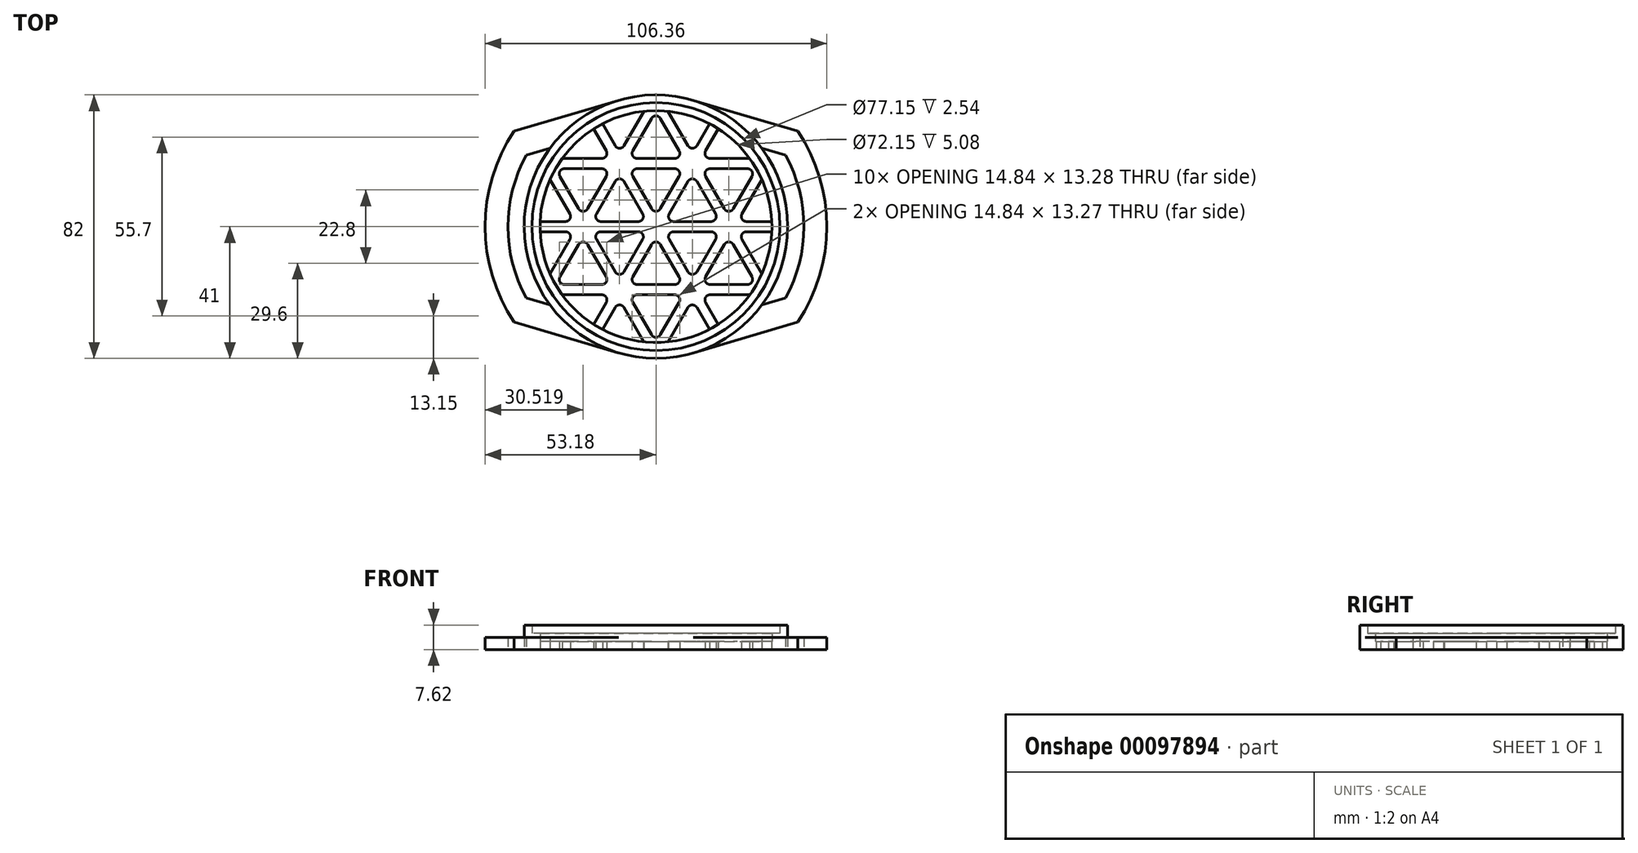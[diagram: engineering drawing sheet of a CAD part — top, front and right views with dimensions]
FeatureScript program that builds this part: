
annotation { "Feature Type Name" : "Feature", "Feature Type Description" : "" }
export const myFeature = defineFeature(function(context is Context, id is Id, definition is map)
    precondition{}
    {
        {
            var Q0;
            Q0=qCreatedBy(makeId("Top.planeOp"),FACE);
            var sketch = newSketch(context, id + "F0", { "sketchPlane" : qUnion([Q0])});
            skCircle(sketch, "E0", {"center": v(0, 0) * mm, "radius": 38.58 * mm});
            skCircle(sketch, "E1", {"center": v(0, 0) * mm, "radius": 41 * mm});
            skCircle(sketch, "E2", {"center": v(0, 0) * mm, "radius": 36.08 * mm});
            skArc(sketch, "E3.cCircle", {"start": v(-7.42, -16.44) * mm, "mid": v(12.1, 13.37) * mm, "end": v(-15.62, -9.02) * mm, "construction": true});
            skLineSegment(sketch, "E3.0", {"start": v(-28.5, 18.04) * mm, "end": v(-16.83, 18.04) * mm});
            skLineSegment(sketch, "E3.1", {"start": v(29.87, 15.66) * mm, "end": v(24.04, 5.56) * mm});
            skLineSegment(sketch, "E3.2", {"start": v(-1.37, -33.7) * mm, "end": v(-7.2, -23.6) * mm});
            skPoint(sketch, "E3.0.midPoint", {"position": v(0, 18.04) * mm});
            skLineSegment(sketch, "E4.0", {"start": v(-36.74, 21.21) * mm, "end": v(-32.22, 21.21) * mm, "construction": true});
            skLineSegment(sketch, "E4.1", {"start": v(0, -42.43) * mm, "end": v(-2.26, -38.5) * mm, "construction": true});
            skLineSegment(sketch, "E4.2", {"start": v(36.74, 21.21) * mm, "end": v(34.48, 17.3) * mm, "construction": true});
            skLineSegment(sketch, "E5", {"start": v(-36.08, 0) * mm, "end": v(36.08, 0) * mm, "construction": true});
            skLineSegment(sketch, "E6.MirrorCS", {"start": v(-36.74, -21.21) * mm, "end": v(-32.22, -21.21) * mm, "construction": true});
            skLineSegment(sketch, "E7.MirrorCS", {"start": v(-28.5, -18.04) * mm, "end": v(-16.83, -18.04) * mm});
            skLineSegment(sketch, "E8.MirrorCS", {"start": v(-1.37, 33.7) * mm, "end": v(-7.2, 23.6) * mm});
            skLineSegment(sketch, "E9.MirrorCS", {"start": v(0, 42.43) * mm, "end": v(-2.26, 38.5) * mm, "construction": true});
            skLineSegment(sketch, "E10.MirrorCS", {"start": v(29.87, -15.66) * mm, "end": v(24.04, -5.56) * mm});
            skLineSegment(sketch, "E11.MirrorCS", {"start": v(36.74, -21.21) * mm, "end": v(34.48, -17.3) * mm, "construction": true});
            skLineSegment(sketch, "E12.trimOffspring", {"start": v(-3.78, 35.88) * mm, "end": v(-9.96, 25.18) * mm});
            skLineSegment(sketch, "E13.trimOffspring", {"start": v(2.26, 38.5) * mm, "end": v(0, 42.43) * mm, "construction": true});
            skLineSegment(sketch, "E14.trimOffspring", {"start": v(-29.18, 21.21) * mm, "end": v(-16.83, 21.21) * mm});
            skLineSegment(sketch, "E15.trimOffspring", {"start": v(-34.48, 17.3) * mm, "end": v(-36.74, 21.21) * mm, "construction": true});
            skLineSegment(sketch, "E16.trimOffspring", {"start": v(-34.48, -17.3) * mm, "end": v(-36.74, -21.21) * mm, "construction": true});
            skLineSegment(sketch, "E17.trimOffspring", {"start": v(-29.18, -21.21) * mm, "end": v(-16.83, -21.21) * mm});
            skLineSegment(sketch, "E18.trimOffspring", {"start": v(32.22, 21.21) * mm, "end": v(36.74, 21.21) * mm, "construction": true});
            skLineSegment(sketch, "E19.trimOffspring", {"start": v(32.96, 14.66) * mm, "end": v(26.79, 3.97) * mm});
            skLineSegment(sketch, "E20.trimOffspring", {"start": v(32.22, -21.21) * mm, "end": v(36.74, -21.21) * mm, "construction": true});
            skLineSegment(sketch, "E21.trimOffspring", {"start": v(32.96, -14.66) * mm, "end": v(26.79, -3.97) * mm});
            skLineSegment(sketch, "E22.trimOffspring", {"start": v(-3.78, -35.88) * mm, "end": v(-9.96, -25.18) * mm});
            skLineSegment(sketch, "E23.trimOffspring", {"start": v(2.26, -38.5) * mm, "end": v(0, -42.43) * mm, "construction": true});
            skLineSegment(sketch, "E24.rect.bottom", {"start": v(-40.32, 22.22) * mm, "end": v(40.32, 22.22) * mm, "construction": true});
            skLineSegment(sketch, "E24.rect.top", {"start": v(-40.32, -22.22) * mm, "end": v(40.32, -22.22) * mm, "construction": true});
            skLineSegment(sketch, "E24.rect.left", {"start": v(-40.32, 22.23) * mm, "end": v(-40.32, -22.23) * mm, "construction": true});
            skLineSegment(sketch, "E24.rect.right", {"start": v(40.32, 22.23) * mm, "end": v(40.32, -22.23) * mm, "construction": true});
            skArc(sketch, "E25", {"start": v(-44.13, 29.68) * mm, "mid": v(-53.18, 0) * mm, "end": v(-44.13, -29.68) * mm});
            skLineSegment(sketch, "E26", {"start": v(-44.13, 29.68) * mm, "end": v(-44.13, -29.68) * mm, "construction": true});
            skLineSegment(sketch, "E27", {"start": v(-44.13, -29.68) * mm, "end": v(-31.73, -33.36) * mm});
            skLineSegment(sketch, "E28", {"start": v(-11.65, 39.3) * mm, "end": v(-31.73, 33.36) * mm});
            skPoint(sketch, "E29.orphan", {"position": v(0, -42.76) * mm});
            skPoint(sketch, "E30.orphan", {"position": v(0, 42.76) * mm});
            skLineSegment(sketch, "E31", {"start": v(-31.73, -33.36) * mm, "end": v(-11.65, -39.3) * mm});
            skLineSegment(sketch, "E32", {"start": v(-31.73, 33.36) * mm, "end": v(-44.13, 29.68) * mm});
            skArc(sketch, "E33", {"start": v(-44.13, -13.12) * mm, "mid": v(-39.25, -24.05) * mm, "end": v(-31.73, -33.36) * mm});
            skArc(sketch, "E34", {"start": v(-44.13, 13.12) * mm, "mid": v(-46.04, 0) * mm, "end": v(-44.13, -13.12) * mm});
            skLineSegment(sketch, "E35", {"start": v(0, 36.07) * mm, "end": v(0, -36.07) * mm, "construction": true});
            skLineSegment(sketch, "E36.MirrorCS", {"start": v(44.13, 29.68) * mm, "end": v(44.13, -29.68) * mm, "construction": true});
            skLineSegment(sketch, "E37.MirrorCS", {"start": v(11.65, 39.3) * mm, "end": v(31.73, 33.36) * mm});
            skLineSegment(sketch, "E38.MirrorCS", {"start": v(31.73, -33.36) * mm, "end": v(11.65, -39.3) * mm});
            skLineSegment(sketch, "E39.MirrorCS", {"start": v(44.13, -29.68) * mm, "end": v(31.73, -33.36) * mm});
            skLineSegment(sketch, "E40.MirrorCS", {"start": v(31.73, 33.36) * mm, "end": v(44.13, 29.68) * mm});
            skArc(sketch, "E41.trimOffspring", {"start": v(-31.73, 33.36) * mm, "mid": v(-39.25, 24.05) * mm, "end": v(-44.13, 13.12) * mm});
            skArc(sketch, "E42.trimOffspring", {"start": v(31.73, -33.36) * mm, "mid": v(46.04, 0) * mm, "end": v(31.73, 33.36) * mm});
            skArc(sketch, "E43.trimOffspring", {"start": v(44.13, -29.68) * mm, "mid": v(53.18, 0) * mm, "end": v(44.13, 29.68) * mm});
            skLineSegment(sketch, "E44", {"start": v(-40.32, 22.22) * mm, "end": v(-32.94, 24.41) * mm});
            skLineSegment(sketch, "E45.MirrorCS", {"start": v(40.32, 22.22) * mm, "end": v(32.94, 24.41) * mm});
            skLineSegment(sketch, "E46.MirrorCS", {"start": v(-40.32, -22.22) * mm, "end": v(-32.94, -24.41) * mm});
            skLineSegment(sketch, "E47.MirrorCS", {"start": v(40.32, -22.22) * mm, "end": v(32.94, -24.41) * mm});
            skLineSegment(sketch, "E48.trimOffspring", {"start": v(-26.79, -3.97) * mm, "end": v(-32.96, -14.66) * mm});
            skLineSegment(sketch, "E49.trimOffspring", {"start": v(-24.04, -5.56) * mm, "end": v(-29.87, -15.66) * mm});
            skLineSegment(sketch, "E50.trimOffspring", {"start": v(-24.04, 5.56) * mm, "end": v(-29.87, 15.66) * mm});
            skLineSegment(sketch, "E51.trimOffspring", {"start": v(-26.79, 3.97) * mm, "end": v(-32.96, 14.66) * mm});
            skLineSegment(sketch, "E52.trimOffspring", {"start": v(-5.83, 18.04) * mm, "end": v(5.83, 18.04) * mm});
            skLineSegment(sketch, "E53.trimOffspring", {"start": v(-5.83, 21.21) * mm, "end": v(5.83, 21.21) * mm});
            skLineSegment(sketch, "E54.trimOffspring", {"start": v(-15.45, 15.66) * mm, "end": v(-21.29, 5.56) * mm});
            skLineSegment(sketch, "E55.trimOffspring", {"start": v(-12.7, 14.07) * mm, "end": v(-18.54, 3.97) * mm});
            skLineSegment(sketch, "E56.trimOffspring", {"start": v(7.2, 23.6) * mm, "end": v(1.37, 33.7) * mm});
            skLineSegment(sketch, "E57.trimOffspring", {"start": v(9.96, 25.18) * mm, "end": v(3.78, 35.88) * mm});
            skLineSegment(sketch, "E58.trimOffspring", {"start": v(16.83, 18.04) * mm, "end": v(28.5, 18.04) * mm});
            skLineSegment(sketch, "E59.trimOffspring", {"start": v(16.83, 21.21) * mm, "end": v(29.18, 21.21) * mm});
            skLineSegment(sketch, "E60.trimOffspring", {"start": v(21.29, -5.56) * mm, "end": v(15.45, -15.66) * mm});
            skLineSegment(sketch, "E61.trimOffspring", {"start": v(18.54, -3.97) * mm, "end": v(12.7, -14.07) * mm});
            skLineSegment(sketch, "E62.trimOffspring", {"start": v(16.83, -21.21) * mm, "end": v(29.18, -21.21) * mm});
            skLineSegment(sketch, "E63.trimOffspring", {"start": v(16.83, -18.04) * mm, "end": v(28.5, -18.04) * mm});
            skLineSegment(sketch, "E64.trimOffspring", {"start": v(-12.7, -14.07) * mm, "end": v(-18.54, -3.97) * mm});
            skLineSegment(sketch, "E65.trimOffspring", {"start": v(-15.45, -15.66) * mm, "end": v(-21.29, -5.56) * mm});
            skLineSegment(sketch, "E66.trimOffspring", {"start": v(-5.83, -18.04) * mm, "end": v(5.83, -18.04) * mm});
            skLineSegment(sketch, "E67.trimOffspring", {"start": v(-5.83, -21.21) * mm, "end": v(5.83, -21.21) * mm});
            skLineSegment(sketch, "E68.trimOffspring", {"start": v(7.2, -23.6) * mm, "end": v(1.37, -33.7) * mm});
            skLineSegment(sketch, "E69.trimOffspring", {"start": v(9.96, -25.18) * mm, "end": v(3.78, -35.88) * mm});
            skLineSegment(sketch, "E70.trimOffspring", {"start": v(18.54, 3.97) * mm, "end": v(12.7, 14.07) * mm});
            skLineSegment(sketch, "E71.trimOffspring", {"start": v(21.29, 5.56) * mm, "end": v(15.45, 15.66) * mm});
            skPoint(sketch, "E72.visualSharp", {"position": v(-31.24, 18.04) * mm});
            skArc(sketch, "E72.filletArc", {"start": v(-28.5, 18.04) * mm, "mid": v(-29.87, 17.24) * mm, "end": v(-29.87, 15.66) * mm});
            skPoint(sketch, "E73.visualSharp", {"position": v(0, 36.07) * mm});
            skArc(sketch, "E73.filletArc", {"start": v(1.37, 33.7) * mm, "mid": v(0, 34.49) * mm, "end": v(-1.37, 33.7) * mm});
            skPoint(sketch, "E74.visualSharp", {"position": v(31.24, 18.04) * mm});
            skArc(sketch, "E74.filletArc", {"start": v(29.87, 15.66) * mm, "mid": v(29.87, 17.24) * mm, "end": v(28.5, 18.04) * mm});
            skPoint(sketch, "E75.visualSharp", {"position": v(31.24, -18.04) * mm});
            skArc(sketch, "E75.filletArc", {"start": v(28.5, -18.04) * mm, "mid": v(29.87, -17.24) * mm, "end": v(29.87, -15.66) * mm});
            skPoint(sketch, "E76.visualSharp", {"position": v(0, -36.07) * mm});
            skArc(sketch, "E76.filletArc", {"start": v(-1.37, -33.7) * mm, "mid": v(0, -34.49) * mm, "end": v(1.37, -33.7) * mm});
            skPoint(sketch, "E77.visualSharp", {"position": v(-31.24, -18.04) * mm});
            skArc(sketch, "E77.filletArc", {"start": v(-29.87, -15.66) * mm, "mid": v(-29.87, -17.24) * mm, "end": v(-28.5, -18.04) * mm});
            skPoint(sketch, "E78.visualSharp", {"position": v(-22.66, -3.18) * mm});
            skArc(sketch, "E78.filletArc", {"start": v(-21.29, -5.56) * mm, "mid": v(-22.66, -4.76) * mm, "end": v(-24.04, -5.56) * mm});
            skPoint(sketch, "E79.visualSharp", {"position": v(-14.08, -18.04) * mm});
            skArc(sketch, "E79.filletArc", {"start": v(-16.83, -18.04) * mm, "mid": v(-15.45, -17.24) * mm, "end": v(-15.45, -15.66) * mm});
            skPoint(sketch, "E80.visualSharp", {"position": v(-12.25, -21.21) * mm});
            skPoint(sketch, "E81.visualSharp", {"position": v(-8.58, -21.21) * mm});
            skArc(sketch, "E81.filletArc", {"start": v(-5.83, -21.21) * mm, "mid": v(-7.2, -22) * mm, "end": v(-7.2, -23.6) * mm});
            skPoint(sketch, "E82.visualSharp", {"position": v(8.58, -21.21) * mm});
            skArc(sketch, "E82.filletArc", {"start": v(7.2, -23.6) * mm, "mid": v(7.2, -22) * mm, "end": v(5.83, -21.21) * mm});
            skPoint(sketch, "E83.visualSharp", {"position": v(14.08, -18.04) * mm});
            skArc(sketch, "E83.filletArc", {"start": v(15.45, -15.66) * mm, "mid": v(15.45, -17.24) * mm, "end": v(16.83, -18.04) * mm});
            skPoint(sketch, "E84.visualSharp", {"position": v(22.66, -3.18) * mm});
            skArc(sketch, "E84.filletArc", {"start": v(24.04, -5.56) * mm, "mid": v(22.66, -4.76) * mm, "end": v(21.29, -5.56) * mm});
            skPoint(sketch, "E85.visualSharp", {"position": v(22.66, 3.18) * mm});
            skArc(sketch, "E85.filletArc", {"start": v(21.29, 5.56) * mm, "mid": v(22.66, 4.76) * mm, "end": v(24.04, 5.56) * mm});
            skPoint(sketch, "E86.visualSharp", {"position": v(8.58, 21.21) * mm});
            skArc(sketch, "E86.filletArc", {"start": v(5.83, 21.21) * mm, "mid": v(7.2, 22) * mm, "end": v(7.2, 23.6) * mm});
            skPoint(sketch, "E87.visualSharp", {"position": v(14.08, 18.04) * mm});
            skArc(sketch, "E87.filletArc", {"start": v(16.83, 18.04) * mm, "mid": v(15.45, 17.24) * mm, "end": v(15.45, 15.66) * mm});
            skPoint(sketch, "E88.visualSharp", {"position": v(-8.58, 21.21) * mm});
            skArc(sketch, "E88.filletArc", {"start": v(-7.2, 23.6) * mm, "mid": v(-7.2, 22) * mm, "end": v(-5.83, 21.21) * mm});
            skPoint(sketch, "E89.visualSharp", {"position": v(-14.08, 18.04) * mm});
            skArc(sketch, "E89.filletArc", {"start": v(-15.45, 15.66) * mm, "mid": v(-15.45, 17.24) * mm, "end": v(-16.83, 18.04) * mm});
            skPoint(sketch, "E90.visualSharp", {"position": v(-22.66, 3.18) * mm});
            skArc(sketch, "E90.filletArc", {"start": v(-24.04, 5.56) * mm, "mid": v(-22.66, 4.76) * mm, "end": v(-21.29, 5.56) * mm});
            skPoint(sketch, "E91.visualSharp", {"position": v(-24.5, 0) * mm});
            skPoint(sketch, "E92.visualSharp", {"position": v(12.25, -21.21) * mm});
            skPoint(sketch, "E93.visualSharp", {"position": v(24.5, 0) * mm});
            skPoint(sketch, "E94.visualSharp", {"position": v(12.25, 21.21) * mm});
            skPoint(sketch, "E95.visualSharp", {"position": v(-12.25, 21.21) * mm});
            skPoint(sketch, "E96.visualSharp", {"position": v(-20.83, 0) * mm});
            skPoint(sketch, "E97.visualSharp", {"position": v(-10.41, 18.04) * mm});
            skPoint(sketch, "E98.visualSharp", {"position": v(10.41, 18.04) * mm});
            skPoint(sketch, "E99.visualSharp", {"position": v(20.83, 0) * mm});
            skPoint(sketch, "E100.visualSharp", {"position": v(10.41, -18.04) * mm});
            skPoint(sketch, "E101.visualSharp", {"position": v(-10.41, -18.04) * mm});
            skLineSegment(sketch, "E102", {"start": v(36.04, 1.59) * mm, "end": v(28.16, 1.59) * mm});
            skLineSegment(sketch, "E103.MirrorCS", {"start": v(36.04, -1.59) * mm, "end": v(28.16, -1.59) * mm});
            skPoint(sketch, "E104.orphan", {"position": v(-38.54, 1.59) * mm});
            skPoint(sketch, "E105.orphan", {"position": v(-38.54, -1.59) * mm});
            skLineSegment(sketch, "E106.1.0", {"start": v(-19.4, 30.42) * mm, "end": v(-15.45, 23.6) * mm});
            skLineSegment(sketch, "E106.1.1", {"start": v(-16.65, 32) * mm, "end": v(-12.7, 25.18) * mm});
            skLineSegment(sketch, "E106.2.0", {"start": v(-16.65, -32) * mm, "end": v(-12.7, -25.18) * mm});
            skLineSegment(sketch, "E106.2.1", {"start": v(-19.4, -30.42) * mm, "end": v(-15.45, -23.6) * mm});
            skLineSegment(sketch, "E107.trimOffspring", {"start": v(1.37, 5.56) * mm, "end": v(7.2, 15.66) * mm});
            skLineSegment(sketch, "E108.trimOffspring", {"start": v(-5.5, 1.59) * mm, "end": v(-17.16, 1.59) * mm});
            skLineSegment(sketch, "E109.trimOffspring", {"start": v(4.12, 3.97) * mm, "end": v(9.96, 14.07) * mm});
            skLineSegment(sketch, "E110.trimOffspring", {"start": v(1.37, -5.56) * mm, "end": v(7.2, -15.66) * mm});
            skLineSegment(sketch, "E111.trimOffspring", {"start": v(-5.5, -1.59) * mm, "end": v(-17.16, -1.59) * mm});
            skLineSegment(sketch, "E112.trimOffspring", {"start": v(4.12, -3.97) * mm, "end": v(9.96, -14.07) * mm});
            skLineSegment(sketch, "E113", {"start": v(-9.96, -14.07) * mm, "end": v(-4.12, -3.97) * mm});
            skLineSegment(sketch, "E114.trimOffspring", {"start": v(-9.96, 14.07) * mm, "end": v(-4.12, 3.97) * mm});
            skLineSegment(sketch, "E115.trimOffspring", {"start": v(-7.2, 15.66) * mm, "end": v(-1.37, 5.56) * mm});
            skLineSegment(sketch, "E116.trimOffspring", {"start": v(12.7, 25.18) * mm, "end": v(16.65, 32) * mm});
            skLineSegment(sketch, "E117.trimOffspring", {"start": v(15.45, 23.6) * mm, "end": v(19.4, 30.42) * mm});
            skLineSegment(sketch, "E118.trimOffspring", {"start": v(17.16, 1.59) * mm, "end": v(5.5, 1.59) * mm});
            skLineSegment(sketch, "E119.trimOffspring", {"start": v(17.16, -1.59) * mm, "end": v(5.5, -1.59) * mm});
            skLineSegment(sketch, "E120.trimOffspring", {"start": v(12.7, -25.18) * mm, "end": v(16.65, -32) * mm});
            skLineSegment(sketch, "E121.trimOffspring", {"start": v(15.45, -23.6) * mm, "end": v(19.4, -30.42) * mm});
            skLineSegment(sketch, "E122.trimOffspring", {"start": v(-7.2, -15.66) * mm, "end": v(-1.37, -5.56) * mm});
            skLineSegment(sketch, "E123.trimOffspring", {"start": v(-28.16, -1.59) * mm, "end": v(-36.04, -1.59) * mm});
            skLineSegment(sketch, "E124.trimOffspring", {"start": v(-28.16, 1.59) * mm, "end": v(-36.04, 1.59) * mm});
            skPoint(sketch, "E125.visualSharp", {"position": v(11.33, 22.8) * mm});
            skArc(sketch, "E125.filletArc", {"start": v(9.96, 25.18) * mm, "mid": v(11.33, 24.39) * mm, "end": v(12.7, 25.18) * mm});
            skPoint(sketch, "E126.visualSharp", {"position": v(25.41, -1.59) * mm});
            skArc(sketch, "E126.filletArc", {"start": v(28.16, -1.59) * mm, "mid": v(26.79, -2.38) * mm, "end": v(26.79, -3.97) * mm});
            skPoint(sketch, "E127.visualSharp", {"position": v(14.08, -21.21) * mm});
            skArc(sketch, "E127.filletArc", {"start": v(16.83, -21.21) * mm, "mid": v(15.45, -22) * mm, "end": v(15.45, -23.6) * mm});
            skPoint(sketch, "E128.visualSharp", {"position": v(-11.33, -22.8) * mm});
            skArc(sketch, "E128.filletArc", {"start": v(-9.96, -25.18) * mm, "mid": v(-11.33, -24.39) * mm, "end": v(-12.7, -25.18) * mm});
            skPoint(sketch, "E129.visualSharp", {"position": v(11.33, -22.8) * mm});
            skArc(sketch, "E129.filletArc", {"start": v(12.7, -25.18) * mm, "mid": v(11.33, -24.39) * mm, "end": v(9.96, -25.18) * mm});
            skPoint(sketch, "E130.visualSharp", {"position": v(-14.08, -21.21) * mm});
            skArc(sketch, "E130.filletArc", {"start": v(-15.45, -23.6) * mm, "mid": v(-15.45, -22) * mm, "end": v(-16.83, -21.21) * mm});
            skPoint(sketch, "E131.visualSharp", {"position": v(-25.41, 1.59) * mm});
            skArc(sketch, "E131.filletArc", {"start": v(-28.16, 1.59) * mm, "mid": v(-26.79, 2.38) * mm, "end": v(-26.79, 3.97) * mm});
            skPoint(sketch, "E132.visualSharp", {"position": v(-25.41, -1.59) * mm});
            skArc(sketch, "E132.filletArc", {"start": v(-26.79, -3.97) * mm, "mid": v(-26.79, -2.38) * mm, "end": v(-28.16, -1.59) * mm});
            skPoint(sketch, "E133.visualSharp", {"position": v(-11.33, 22.8) * mm});
            skArc(sketch, "E133.filletArc", {"start": v(-12.7, 25.18) * mm, "mid": v(-11.33, 24.39) * mm, "end": v(-9.96, 25.18) * mm});
            skPoint(sketch, "E134.visualSharp", {"position": v(-14.08, 21.21) * mm});
            skArc(sketch, "E134.filletArc", {"start": v(-16.83, 21.21) * mm, "mid": v(-15.45, 22) * mm, "end": v(-15.45, 23.6) * mm});
            skPoint(sketch, "E135.visualSharp", {"position": v(14.08, 21.21) * mm});
            skArc(sketch, "E135.filletArc", {"start": v(15.45, 23.6) * mm, "mid": v(15.45, 22) * mm, "end": v(16.83, 21.21) * mm});
            skPoint(sketch, "E136.visualSharp", {"position": v(25.41, 1.59) * mm});
            skArc(sketch, "E136.filletArc", {"start": v(26.79, 3.97) * mm, "mid": v(26.79, 2.38) * mm, "end": v(28.16, 1.59) * mm});
            skPoint(sketch, "E137.visualSharp", {"position": v(11.33, -16.45) * mm});
            skArc(sketch, "E137.filletArc", {"start": v(9.96, -14.07) * mm, "mid": v(11.33, -14.86) * mm, "end": v(12.7, -14.07) * mm});
            skPoint(sketch, "E138.visualSharp", {"position": v(2.75, -1.59) * mm});
            skArc(sketch, "E138.filletArc", {"start": v(5.5, -1.59) * mm, "mid": v(4.12, -2.38) * mm, "end": v(4.12, -3.97) * mm});
            skPoint(sketch, "E139.visualSharp", {"position": v(19.91, -1.59) * mm});
            skArc(sketch, "E139.filletArc", {"start": v(18.54, -3.97) * mm, "mid": v(18.54, -2.38) * mm, "end": v(17.16, -1.59) * mm});
            skPoint(sketch, "E140.visualSharp", {"position": v(19.91, 1.59) * mm});
            skArc(sketch, "E140.filletArc", {"start": v(17.16, 1.59) * mm, "mid": v(18.54, 2.38) * mm, "end": v(18.54, 3.97) * mm});
            skPoint(sketch, "E141.visualSharp", {"position": v(11.33, 16.45) * mm});
            skArc(sketch, "E141.filletArc", {"start": v(12.7, 14.07) * mm, "mid": v(11.33, 14.86) * mm, "end": v(9.96, 14.07) * mm});
            skPoint(sketch, "E142.visualSharp", {"position": v(2.75, 1.59) * mm});
            skArc(sketch, "E142.filletArc", {"start": v(4.12, 3.97) * mm, "mid": v(4.12, 2.38) * mm, "end": v(5.5, 1.59) * mm});
            skPoint(sketch, "E143.visualSharp", {"position": v(8.58, 18.04) * mm});
            skArc(sketch, "E143.filletArc", {"start": v(7.2, 15.66) * mm, "mid": v(7.2, 17.24) * mm, "end": v(5.83, 18.04) * mm});
            skPoint(sketch, "E144.visualSharp", {"position": v(-8.58, 18.04) * mm});
            skArc(sketch, "E144.filletArc", {"start": v(-5.83, 18.04) * mm, "mid": v(-7.2, 17.24) * mm, "end": v(-7.2, 15.66) * mm});
            skPoint(sketch, "E145.visualSharp", {"position": v(0, 3.17) * mm});
            skArc(sketch, "E145.filletArc", {"start": v(-1.37, 5.56) * mm, "mid": v(0, 4.76) * mm, "end": v(1.37, 5.56) * mm});
            skPoint(sketch, "E146.visualSharp", {"position": v(-2.75, 1.59) * mm});
            skArc(sketch, "E146.filletArc", {"start": v(-5.5, 1.59) * mm, "mid": v(-4.12, 2.38) * mm, "end": v(-4.12, 3.97) * mm});
            skPoint(sketch, "E147.visualSharp", {"position": v(-11.33, 16.45) * mm});
            skArc(sketch, "E147.filletArc", {"start": v(-9.96, 14.07) * mm, "mid": v(-11.33, 14.86) * mm, "end": v(-12.7, 14.07) * mm});
            skPoint(sketch, "E148.visualSharp", {"position": v(-19.91, 1.59) * mm});
            skArc(sketch, "E148.filletArc", {"start": v(-18.54, 3.97) * mm, "mid": v(-18.54, 2.38) * mm, "end": v(-17.16, 1.59) * mm});
            skPoint(sketch, "E149.visualSharp", {"position": v(-2.75, -1.59) * mm});
            skArc(sketch, "E149.filletArc", {"start": v(-4.12, -3.97) * mm, "mid": v(-4.12, -2.38) * mm, "end": v(-5.5, -1.59) * mm});
            skPoint(sketch, "E150.visualSharp", {"position": v(-19.91, -1.59) * mm});
            skArc(sketch, "E150.filletArc", {"start": v(-17.16, -1.59) * mm, "mid": v(-18.54, -2.38) * mm, "end": v(-18.54, -3.97) * mm});
            skPoint(sketch, "E151.visualSharp", {"position": v(-8.58, -18.04) * mm});
            skArc(sketch, "E151.filletArc", {"start": v(-7.2, -15.66) * mm, "mid": v(-7.2, -17.24) * mm, "end": v(-5.83, -18.04) * mm});
            skPoint(sketch, "E152.visualSharp", {"position": v(0, -3.18) * mm});
            skArc(sketch, "E152.filletArc", {"start": v(1.37, -5.56) * mm, "mid": v(0, -4.76) * mm, "end": v(-1.37, -5.56) * mm});
            skPoint(sketch, "E153.visualSharp", {"position": v(8.58, -18.04) * mm});
            skArc(sketch, "E153.filletArc", {"start": v(5.83, -18.04) * mm, "mid": v(7.2, -17.24) * mm, "end": v(7.2, -15.66) * mm});
            skArc(sketch, "E154.filletArc", {"start": v(-12.7, -14.07) * mm, "mid": v(-11.33, -14.86) * mm, "end": v(-9.96, -14.07) * mm});
            skCircle(sketch, "E155", {"center": v(0, 0) * mm, "radius": 6.35 * mm, "construction": true});
            skSolve(sketch);
        }
        {
            var Q0;
            Q0=makeQuery(id+"F0.imprint","IMPRINT",FACE,{"disambiguationData":[TD([[makeQuery(id+"F0.imprint","IMPRINT",EDGE,{"derivedFrom":sQuery(id+"F0.wireOp",EDGE,"E0")}),-1.0]])]});
            extrude(context, id + "F1", {"entities" : qUnion([Q0]), "depth" : 7.62 * mm});
        }
        {
            var Q0;
            Q0=makeQuery(id+"F0.imprint","IMPRINT",FACE,{"disambiguationData":[TD([[makeQuery(id+"F0.imprint","IMPRINT",EDGE,{"derivedFrom":sQuery(id+"F0.wireOp",EDGE,"E0")}),1.0]])]});
            extrude(context, id + "F2", {"entities" : qUnion([Q0]), "operationType" : NewBodyOperationType.ADD, "depth" : 5.08 * mm});
        }
        {
            var Q0;
            {var subQ22=sQuery(id+"F0.wireOp",EDGE,"E3.0");Q0=makeQuery(id+"F0.imprint","IMPRINT",FACE,{"disambiguationData":[TD([[makeQuery(id+"F0.imprint","IMPRINT",EDGE,{"derivedFrom":subQ22}),1.0]])]});}
            var Q1;
            Q1=makeQuery(id+"F0.imprint","IMPRINT",FACE,{"disambiguationData":[TD([[makeQuery(id+"F0.imprint","IMPRINT",EDGE,{"derivedFrom":sQuery(id+"F0.wireOp",EDGE,"E25")}),1.0]])]});
            var Q2;
            {var subQ2=sQuery(id+"F0.wireOp",EDGE,"E31");Q2=makeQuery(id+"F0.imprint","IMPRINT",FACE,{"disambiguationData":[TD([[makeQuery(id+"F0.imprint","IMPRINT",EDGE,{"derivedFrom":subQ2}),1.0]])]});}
            var Q3;
            {var subQ2=sQuery(id+"F0.wireOp",EDGE,"E28");Q3=makeQuery(id+"F0.imprint","IMPRINT",FACE,{"disambiguationData":[TD([[makeQuery(id+"F0.imprint","IMPRINT",EDGE,{"derivedFrom":subQ2}),1.0]])]});}
            var Q4;
            {var subQ2=sQuery(id+"F0.wireOp",EDGE,"E37.MirrorCS");Q4=makeQuery(id+"F0.imprint","IMPRINT",FACE,{"disambiguationData":[TD([[makeQuery(id+"F0.imprint","IMPRINT",EDGE,{"derivedFrom":subQ2}),-1.0]])]});}
            var Q5;
            {var subQ4=sQuery(id+"F0.wireOp",EDGE,"E39.MirrorCS");Q5=makeQuery(id+"F0.imprint","IMPRINT",FACE,{"disambiguationData":[TD([[makeQuery(id+"F0.imprint","IMPRINT",EDGE,{"derivedFrom":subQ4}),-1.0]])]});}
            var Q6;
            {var subQ2=sQuery(id+"F0.wireOp",EDGE,"E38.MirrorCS");Q6=makeQuery(id+"F0.imprint","IMPRINT",FACE,{"disambiguationData":[TD([[makeQuery(id+"F0.imprint","IMPRINT",EDGE,{"derivedFrom":subQ2}),-1.0]])]});}
            extrude(context, id + "F3", {"entities" : qUnion([Q0, Q1, Q2, Q3, Q4, Q5, Q6]), "operationType" : NewBodyOperationType.ADD, "depth" : 3.8 * mm});
        }
        {
            var Q0;
            Q0=makeQuery(id+"F3.opExtrude","CAP_FACE",FACE,{"disambiguationData":[OSD([sQuery(id+"F0.wireOp",EDGE,"E2"),sQuery(id+"F0.wireOp",EDGE,"E3.0"),sQuery(id+"F0.wireOp",EDGE,"E3.1"),sQuery(id+"F0.wireOp",EDGE,"E3.2"),sQuery(id+"F0.wireOp",EDGE,"E7.MirrorCS"),sQuery(id+"F0.wireOp",EDGE,"E8.MirrorCS"),sQuery(id+"F0.wireOp",EDGE,"E10.MirrorCS"),sQuery(id+"F0.wireOp",EDGE,"E12.trimOffspring"),sQuery(id+"F0.wireOp",EDGE,"E14.trimOffspring"),sQuery(id+"F0.wireOp",EDGE,"E17.trimOffspring"),sQuery(id+"F0.wireOp",EDGE,"E19.trimOffspring"),sQuery(id+"F0.wireOp",EDGE,"E21.trimOffspring"),sQuery(id+"F0.wireOp",EDGE,"E22.trimOffspring"),sQuery(id+"F0.wireOp",EDGE,"E48.trimOffspring"),sQuery(id+"F0.wireOp",EDGE,"E49.trimOffspring"),sQuery(id+"F0.wireOp",EDGE,"E50.trimOffspring"),sQuery(id+"F0.wireOp",EDGE,"E51.trimOffspring"),sQuery(id+"F0.wireOp",EDGE,"E52.trimOffspring"),sQuery(id+"F0.wireOp",EDGE,"E53.trimOffspring"),sQuery(id+"F0.wireOp",EDGE,"E54.trimOffspring"),sQuery(id+"F0.wireOp",EDGE,"E55.trimOffspring"),sQuery(id+"F0.wireOp",EDGE,"E56.trimOffspring"),sQuery(id+"F0.wireOp",EDGE,"E57.trimOffspring"),sQuery(id+"F0.wireOp",EDGE,"E58.trimOffspring"),sQuery(id+"F0.wireOp",EDGE,"E59.trimOffspring"),sQuery(id+"F0.wireOp",EDGE,"E60.trimOffspring"),sQuery(id+"F0.wireOp",EDGE,"E61.trimOffspring"),sQuery(id+"F0.wireOp",EDGE,"E62.trimOffspring"),sQuery(id+"F0.wireOp",EDGE,"E63.trimOffspring"),sQuery(id+"F0.wireOp",EDGE,"E64.trimOffspring"),sQuery(id+"F0.wireOp",EDGE,"E65.trimOffspring"),sQuery(id+"F0.wireOp",EDGE,"E66.trimOffspring"),sQuery(id+"F0.wireOp",EDGE,"E67.trimOffspring"),sQuery(id+"F0.wireOp",EDGE,"E68.trimOffspring"),sQuery(id+"F0.wireOp",EDGE,"E69.trimOffspring"),sQuery(id+"F0.wireOp",EDGE,"E70.trimOffspring"),sQuery(id+"F0.wireOp",EDGE,"E71.trimOffspring"),sQuery(id+"F0.wireOp",EDGE,"E72.filletArc"),sQuery(id+"F0.wireOp",EDGE,"E73.filletArc"),sQuery(id+"F0.wireOp",EDGE,"E74.filletArc"),sQuery(id+"F0.wireOp",EDGE,"E75.filletArc"),sQuery(id+"F0.wireOp",EDGE,"E76.filletArc"),sQuery(id+"F0.wireOp",EDGE,"E77.filletArc"),sQuery(id+"F0.wireOp",EDGE,"E78.filletArc"),sQuery(id+"F0.wireOp",EDGE,"E79.filletArc"),sQuery(id+"F0.wireOp",EDGE,"E81.filletArc"),sQuery(id+"F0.wireOp",EDGE,"E82.filletArc"),sQuery(id+"F0.wireOp",EDGE,"E83.filletArc"),sQuery(id+"F0.wireOp",EDGE,"E84.filletArc"),sQuery(id+"F0.wireOp",EDGE,"E85.filletArc"),sQuery(id+"F0.wireOp",EDGE,"E86.filletArc"),sQuery(id+"F0.wireOp",EDGE,"E87.filletArc"),sQuery(id+"F0.wireOp",EDGE,"E88.filletArc"),sQuery(id+"F0.wireOp",EDGE,"E89.filletArc"),sQuery(id+"F0.wireOp",EDGE,"E90.filletArc"),sQuery(id+"F0.wireOp",EDGE,"E102"),sQuery(id+"F0.wireOp",EDGE,"E103.MirrorCS"),sQuery(id+"F0.wireOp",EDGE,"E106.1.0"),sQuery(id+"F0.wireOp",EDGE,"E106.1.1"),sQuery(id+"F0.wireOp",EDGE,"E106.2.0"),sQuery(id+"F0.wireOp",EDGE,"E106.2.1"),sQuery(id+"F0.wireOp",EDGE,"E107.trimOffspring"),sQuery(id+"F0.wireOp",EDGE,"E108.trimOffspring"),sQuery(id+"F0.wireOp",EDGE,"E109.trimOffspring"),sQuery(id+"F0.wireOp",EDGE,"E110.trimOffspring"),sQuery(id+"F0.wireOp",EDGE,"E111.trimOffspring"),sQuery(id+"F0.wireOp",EDGE,"E112.trimOffspring"),sQuery(id+"F0.wireOp",EDGE,"E113"),sQuery(id+"F0.wireOp",EDGE,"E114.trimOffspring"),sQuery(id+"F0.wireOp",EDGE,"E115.trimOffspring"),sQuery(id+"F0.wireOp",EDGE,"E116.trimOffspring"),sQuery(id+"F0.wireOp",EDGE,"E117.trimOffspring"),sQuery(id+"F0.wireOp",EDGE,"E118.trimOffspring"),sQuery(id+"F0.wireOp",EDGE,"E119.trimOffspring"),sQuery(id+"F0.wireOp",EDGE,"E120.trimOffspring"),sQuery(id+"F0.wireOp",EDGE,"E121.trimOffspring"),sQuery(id+"F0.wireOp",EDGE,"E122.trimOffspring"),sQuery(id+"F0.wireOp",EDGE,"E123.trimOffspring"),sQuery(id+"F0.wireOp",EDGE,"E124.trimOffspring"),sQuery(id+"F0.wireOp",EDGE,"E125.filletArc"),sQuery(id+"F0.wireOp",EDGE,"E126.filletArc"),sQuery(id+"F0.wireOp",EDGE,"E127.filletArc"),sQuery(id+"F0.wireOp",EDGE,"E128.filletArc"),sQuery(id+"F0.wireOp",EDGE,"E129.filletArc"),sQuery(id+"F0.wireOp",EDGE,"E130.filletArc"),sQuery(id+"F0.wireOp",EDGE,"E131.filletArc"),sQuery(id+"F0.wireOp",EDGE,"E132.filletArc"),sQuery(id+"F0.wireOp",EDGE,"E133.filletArc"),sQuery(id+"F0.wireOp",EDGE,"E134.filletArc"),sQuery(id+"F0.wireOp",EDGE,"E135.filletArc"),sQuery(id+"F0.wireOp",EDGE,"E136.filletArc"),sQuery(id+"F0.wireOp",EDGE,"E137.filletArc"),sQuery(id+"F0.wireOp",EDGE,"E138.filletArc"),sQuery(id+"F0.wireOp",EDGE,"E139.filletArc"),sQuery(id+"F0.wireOp",EDGE,"E140.filletArc"),sQuery(id+"F0.wireOp",EDGE,"E141.filletArc"),sQuery(id+"F0.wireOp",EDGE,"E142.filletArc"),sQuery(id+"F0.wireOp",EDGE,"E143.filletArc"),sQuery(id+"F0.wireOp",EDGE,"E144.filletArc"),sQuery(id+"F0.wireOp",EDGE,"E145.filletArc"),sQuery(id+"F0.wireOp",EDGE,"E146.filletArc"),sQuery(id+"F0.wireOp",EDGE,"E147.filletArc"),sQuery(id+"F0.wireOp",EDGE,"E148.filletArc"),sQuery(id+"F0.wireOp",EDGE,"E149.filletArc"),sQuery(id+"F0.wireOp",EDGE,"E150.filletArc"),sQuery(id+"F0.wireOp",EDGE,"E151.filletArc"),sQuery(id+"F0.wireOp",EDGE,"E152.filletArc"),sQuery(id+"F0.wireOp",EDGE,"E153.filletArc"),sQuery(id+"F0.wireOp",EDGE,"E154.filletArc")])],"isStart":false});
            var sketch = newSketch(context, id + "F4", { "sketchPlane" : qUnion([Q0])});
            skCircle(sketch, "E156", {"center": v(0, 0) * mm, "radius": 36.08 * mm});
            skSolve(sketch);
        }
        {
            var Q0;
            Q0=qSketchRegion(id+"F4",true);
            extrude(context, id + "F5", {"entities" : qUnion([Q0]), "operationType" : NewBodyOperationType.REMOVE, "oppositeDirection" : true, "depth" : 1.27 * mm});
        }
    });
